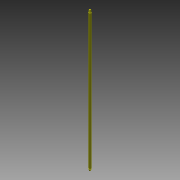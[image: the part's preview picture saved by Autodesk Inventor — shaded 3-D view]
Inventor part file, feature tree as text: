
AUTODESK INVENTOR PART (.ipt)
format: ipt  version: 2015 (Build 190159000, 159)  size: 83,456 bytes
history: native  units: mm
features: sketch x2, extrude x1, revolve x1, mirror x1
ambient origin geometry x8: Origin, YZ Plane, XZ Plane, XY Plane, X Axis, Y Axis, Z Axis, Center Point
bodies: 实体1 (feature_tree)
feature tree (5):
  extrude  "拉伸1"  Depth=10.0mm TaperAngle=0.0deg
  revolve  "旋转1"  [1 undecoded]
  mirror  "镜像1"
  sketch  "草图1"  dims[d0=10.0mm d1=530.0mm d2=0.0mm]
  sketch  "草图2"  dims[d4=2.0mm d5=2.0mm d7=10.0mm d9=90.0deg d10=5.0mm d11=3.0mm]
note: 1 required parameter value undecoded (feature->parameter linkage not recoverable at this tier; creation-order binding heuristic only, values carry confidence <= 0.55)
